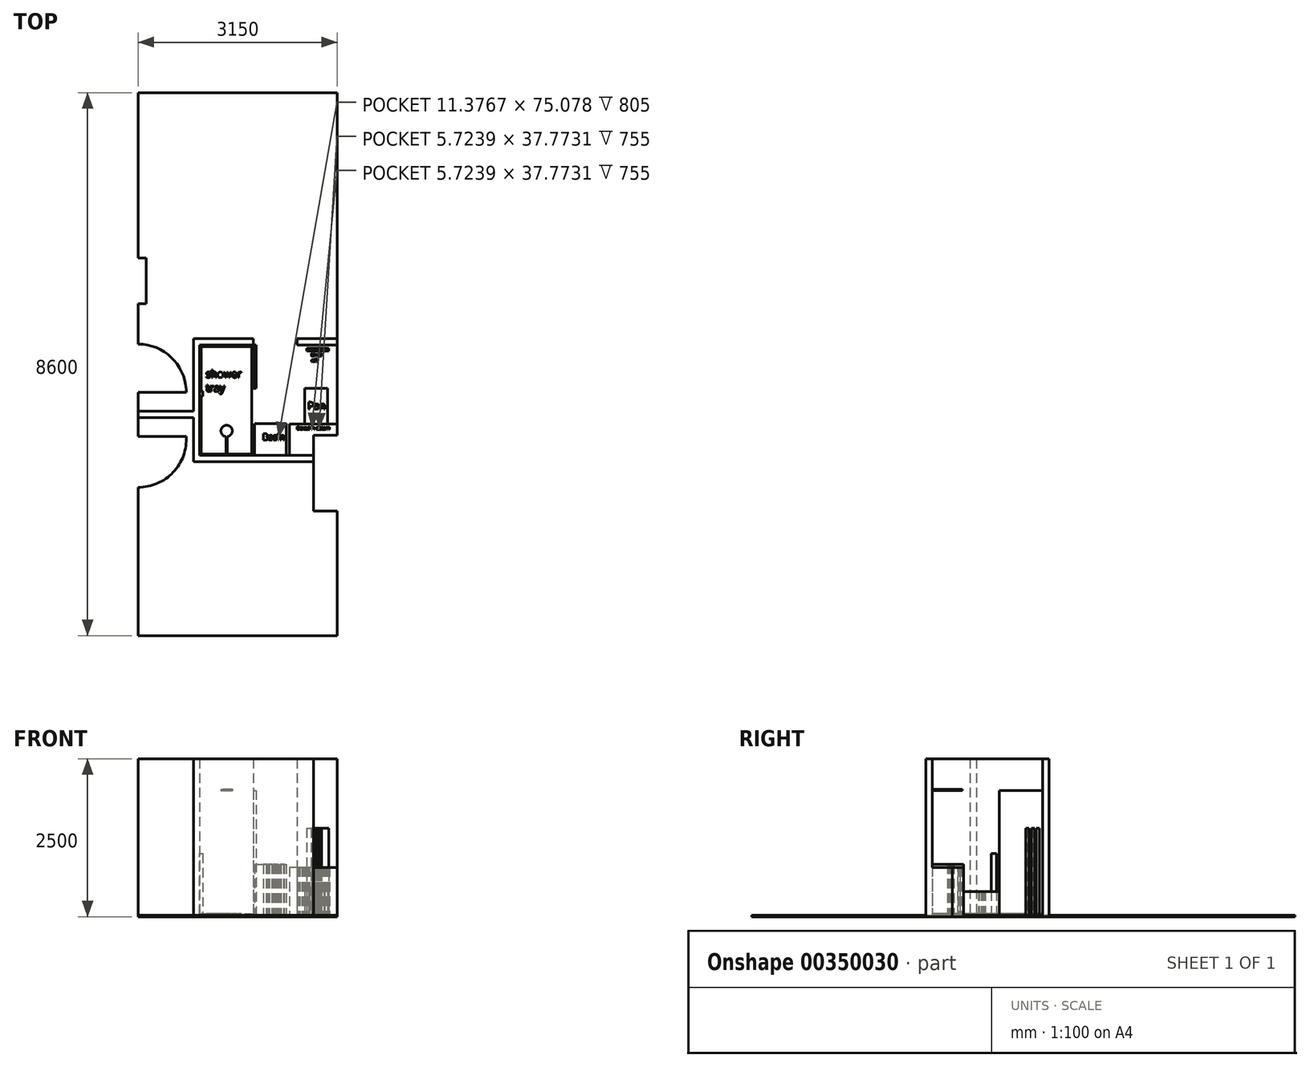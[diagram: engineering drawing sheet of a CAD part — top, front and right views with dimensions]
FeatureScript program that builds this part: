
annotation { "Feature Type Name" : "Feature", "Feature Type Description" : "" }
export const myFeature = defineFeature(function(context is Context, id is Id, definition is map)
    precondition{}
    {
        {
            var Q0;
            Q0=qCreatedBy(makeId("Top.planeOp"),FACE);
            var sketch = newSketch(context, id + "F0", { "sketchPlane" : qUnion([Q0])});
            skLineSegment(sketch, "E0", {"start": v(0, 1108.57) * mm, "end": v(3150, 1108.57) * mm});
            skLineSegment(sketch, "E1", {"start": v(3150, 1108.57) * mm, "end": v(3150, 3083.57) * mm});
            skLineSegment(sketch, "E2", {"start": v(3150, 3083.57) * mm, "end": v(2775, 3083.57) * mm});
            skLineSegment(sketch, "E3", {"start": v(2775, 3083.57) * mm, "end": v(2775, 4283.57) * mm});
            skLineSegment(sketch, "E4", {"start": v(2775, 4283.57) * mm, "end": v(3150, 4283.57) * mm});
            skLineSegment(sketch, "E5", {"start": v(3150, 4283.57) * mm, "end": v(3150, 9708.57) * mm});
            skLineSegment(sketch, "E6", {"start": v(3150, 9708.57) * mm, "end": v(0, 9708.57) * mm});
            skLineSegment(sketch, "E7", {"start": v(0, 9708.57) * mm, "end": v(0, 7088.57) * mm});
            skLineSegment(sketch, "E8", {"start": v(0, 7088.57) * mm, "end": v(125, 7088.57) * mm});
            skLineSegment(sketch, "E9", {"start": v(125, 7088.57) * mm, "end": v(125, 6363.57) * mm});
            skLineSegment(sketch, "E10", {"start": v(125, 6363.57) * mm, "end": v(0, 6363.57) * mm});
            skLineSegment(sketch, "E11", {"start": v(0, 3501.57) * mm, "end": v(0, 1108.57) * mm});
            skLineSegment(sketch, "E12.bottom", {"start": v(0, 4263.57) * mm, "end": v(762, 4263.57) * mm});
            skLineSegment(sketch, "E12.top", {"start": v(0, 4221.57) * mm, "end": v(762, 4221.57) * mm});
            skLineSegment(sketch, "E12.left", {"start": v(0, 4263.57) * mm, "end": v(0, 4221.57) * mm});
            skLineSegment(sketch, "E12.right", {"start": v(762, 4263.57) * mm, "end": v(762, 4221.57) * mm});
            skArc(sketch, "E13", {"start": v(762, 4263.57) * mm, "mid": v(554.28, 3697) * mm, "end": v(0, 3458.41) * mm});
            skLineSegment(sketch, "E14", {"start": v(0, 6363.57) * mm, "end": v(0, 5725.57) * mm});
            skLineSegment(sketch, "E15", {"start": v(0, 4963.57) * mm, "end": v(0, 4263.57) * mm});
            skLineSegment(sketch, "E16.bottom", {"start": v(0, 4963.57) * mm, "end": v(762, 4963.57) * mm});
            skLineSegment(sketch, "E16.top", {"start": v(0, 5005.57) * mm, "end": v(762, 5005.57) * mm});
            skLineSegment(sketch, "E16.left", {"start": v(0, 4963.57) * mm, "end": v(0, 5005.57) * mm});
            skLineSegment(sketch, "E16.right", {"start": v(762, 4963.57) * mm, "end": v(762, 5005.57) * mm});
            skArc(sketch, "E17", {"start": v(762, 4963.57) * mm, "mid": v(538.82, 5502.39) * mm, "end": v(0, 5725.57) * mm});
            skSolve(sketch);
        }
        {
            var Q0;
            Q0=qCreatedBy(makeId("Top.planeOp"),FACE);
            var sketch = newSketch(context, id + "F1", { "sketchPlane" : qUnion([Q0])});
            skLineSegment(sketch, "E18", {"start": v(2775, 3963.57) * mm, "end": v(975, 3963.57) * mm});
            skLineSegment(sketch, "E19", {"start": v(975, 3963.57) * mm, "end": v(975, 5713.57) * mm});
            skLineSegment(sketch, "E20", {"start": v(975, 5713.57) * mm, "end": v(1825, 5713.57) * mm});
            skLineSegment(sketch, "E21.0", {"start": v(875, 3863.57) * mm, "end": v(875, 4563.57) * mm});
            skLineSegment(sketch, "E22.0", {"start": v(2775, 3863.57) * mm, "end": v(875, 3863.57) * mm});
            skLineSegment(sketch, "E23", {"start": v(875, 5813.57) * mm, "end": v(1825, 5813.57) * mm});
            skLineSegment(sketch, "E24", {"start": v(2775, 3963.57) * mm, "end": v(2775, 3863.57) * mm});
            skLineSegment(sketch, "E25.bottom", {"start": v(0, 4663.57) * mm, "end": v(875, 4663.57) * mm});
            skLineSegment(sketch, "E25.top", {"start": v(0, 4563.57) * mm, "end": v(875, 4563.57) * mm});
            skLineSegment(sketch, "E25.left", {"start": v(0, 4663.57) * mm, "end": v(0, 4563.57) * mm});
            skLineSegment(sketch, "E26.trimOffspring", {"start": v(875, 4663.57) * mm, "end": v(875, 5813.57) * mm});
            skLineSegment(sketch, "E27", {"start": v(1825, 5813.57) * mm, "end": v(1825, 5713.57) * mm});
            skSolve(sketch);
        }
        {
            var Q0;
            Q0=qCreatedBy(makeId("Top.planeOp"),FACE);
            var sketch = newSketch(context, id + "F2", { "sketchPlane" : qUnion([Q0])});
            skLineSegment(sketch, "E28.bottom", {"start": v(2515, 5813.57) * mm, "end": v(3150, 5813.57) * mm});
            skLineSegment(sketch, "E28.top", {"start": v(2515, 5713.57) * mm, "end": v(3150, 5713.57) * mm});
            skLineSegment(sketch, "E28.left", {"start": v(2515, 5813.57) * mm, "end": v(2515, 5713.57) * mm});
            skLineSegment(sketch, "E28.right", {"start": v(3150, 5813.57) * mm, "end": v(3150, 5713.57) * mm});
            skSolve(sketch);
        }
        {
            var Q0;
            Q0=qCreatedBy(makeId("Top.planeOp"),FACE);
            cPlane(context, id + "F3", {"entities" : qUnion([Q0]), "cplaneType" : CPlaneType.OFFSET, "offset" : 2000 * mm, "width" : 150 * mm, "height" : 150 * mm});
        }
        {
            var Q0;
            Q0=qCreatedBy(makeId("Top.planeOp"),FACE);
            var sketch = newSketch(context, id + "F4", { "sketchPlane" : qUnion([Q0])});
            skLineSegment(sketch, "E29.bottom", {"start": v(1825, 5713.57) * mm, "end": v(1867, 5713.57) * mm});
            skLineSegment(sketch, "E29.top", {"start": v(1825, 5023.57) * mm, "end": v(1867, 5023.57) * mm});
            skLineSegment(sketch, "E29.left", {"start": v(1825, 5713.57) * mm, "end": v(1825, 5023.57) * mm});
            skLineSegment(sketch, "E29.right", {"start": v(1867, 5713.57) * mm, "end": v(1867, 5023.57) * mm});
            skArc(sketch, "E30", {"start": v(1825, 5023.57) * mm, "mid": v(2312.9, 5225.67) * mm, "end": v(2515, 5713.57) * mm, "construction": true});
            skSolve(sketch);
        }
        {
            var Q0;
            Q0=qCreatedBy(makeId("Top.planeOp"),FACE);
            var sketch = newSketch(context, id + "F5", { "sketchPlane" : qUnion([Q0])});
            skLineSegment(sketch, "E31.bottom", {"start": v(995, 5683.57) * mm, "end": v(1795, 5683.57) * mm});
            skLineSegment(sketch, "E31.top", {"start": v(995, 3983.57) * mm, "end": v(1795, 3983.57) * mm});
            skLineSegment(sketch, "E31.left", {"start": v(995, 5683.57) * mm, "end": v(995, 3983.57) * mm});
            skLineSegment(sketch, "E31.right", {"start": v(1795, 5683.57) * mm, "end": v(1795, 3983.57) * mm});
            skText(sketch, "E32", { "text": "shower\ntray", "fontName": "OpenSans-Regular.ttf"});
            const initialGuessF5  = {"E32": [1.0738, 5.19529, 1, 0, 0.11732]};
            skSetInitialGuess(sketch, initialGuessF5);
            skSolve(sketch);
        }
        {
            var Q0;
            Q0=qCreatedBy(makeId("Top.planeOp"),FACE);
            var sketch = newSketch(context, id + "F6", { "sketchPlane" : qUnion([Q0])});
            skLineSegment(sketch, "E33.bottom", {"start": v(3000, 4458.57) * mm, "end": v(2635, 4458.57) * mm});
            skLineSegment(sketch, "E33.top", {"start": v(3000, 5023.57) * mm, "end": v(2635, 5023.57) * mm});
            skLineSegment(sketch, "E33.left", {"start": v(3000, 4458.57) * mm, "end": v(3000, 5023.57) * mm});
            skLineSegment(sketch, "E33.right", {"start": v(2635, 4458.57) * mm, "end": v(2635, 5023.57) * mm});
            skText(sketch, "E34", { "text": "Pan", "fontName": "OpenSans-Regular.ttf"});
            const initialGuessF6  = {"E34": [2.6861, 4.69488, 1, 0, 0.11267]};
            skSetInitialGuess(sketch, initialGuessF6);
            skSolve(sketch);
        }
        {
            var Q0;
            Q0=qCreatedBy(makeId("Top.planeOp"),FACE);
            var sketch = newSketch(context, id + "F7", { "sketchPlane" : qUnion([Q0])});
            skLineSegment(sketch, "E35.bottom", {"start": v(1845, 3963.57) * mm, "end": v(2345, 3963.57) * mm});
            skLineSegment(sketch, "E35.top", {"start": v(1845, 4463.57) * mm, "end": v(2345, 4463.57) * mm});
            skLineSegment(sketch, "E35.left", {"start": v(1845, 3963.57) * mm, "end": v(1845, 4463.57) * mm});
            skLineSegment(sketch, "E35.right", {"start": v(2345, 3963.57) * mm, "end": v(2345, 4463.57) * mm});
            skText(sketch, "E36", { "text": "Basin", "fontName": "OpenSans-Regular.ttf"});
            const initialGuessF7  = {"E36": [1.96667, 4.20594, 1, 0, 0.10101]};
            skSetInitialGuess(sketch, initialGuessF7);
            skSolve(sketch);
        }
        {
            var Q0;
            Q0=qCreatedBy(makeId("Top.planeOp"),FACE);
            var sketch = newSketch(context, id + "F8", { "sketchPlane" : qUnion([Q0])});
            skLineSegment(sketch, "E37", {"start": v(3150, 4458.57) * mm, "end": v(2395, 4458.57) * mm});
            skLineSegment(sketch, "E38", {"start": v(2395, 4458.57) * mm, "end": v(2395, 3963.57) * mm});
            skText(sketch, "E39", { "text": "Boxed in cistern", "fontName": "OpenSans-Regular.ttf"});
            skLineSegment(sketch, "E40", {"start": v(3150, 4458.57) * mm, "end": v(3150, 4283.57) * mm});
            skLineSegment(sketch, "E41", {"start": v(3150, 4283.57) * mm, "end": v(2775, 4283.57) * mm});
            skLineSegment(sketch, "E42", {"start": v(2775, 4283.57) * mm, "end": v(2775, 3963.57) * mm});
            skLineSegment(sketch, "E43", {"start": v(2775, 3963.57) * mm, "end": v(2395, 3963.57) * mm});
            const initialGuessF8  = {"E39": [2.50984, 4.37021, 1, 0, 0.05082]};
            skSetInitialGuess(sketch, initialGuessF8);
            skSolve(sketch);
        }
        {
            var Q0;
            Q0=qCreatedBy(makeId("Top.planeOp"),FACE);
            var sketch = newSketch(context, id + "F9", { "sketchPlane" : qUnion([Q0])});
            skLineSegment(sketch, "E44.bottom", {"start": v(2670, 5663.57) * mm, "end": v(3020, 5663.57) * mm});
            skLineSegment(sketch, "E44.top", {"start": v(2670, 5613.57) * mm, "end": v(3020, 5613.57) * mm});
            skLineSegment(sketch, "E44.left", {"start": v(2670, 5663.57) * mm, "end": v(2670, 5613.57) * mm});
            skLineSegment(sketch, "E44.right", {"start": v(3020, 5663.57) * mm, "end": v(3020, 5613.57) * mm});
            skText(sketch, "E45", { "text": "towel\nrail", "fontName": "OpenSans-Regular.ttf"});
            const initialGuessF9  = {"E45": [2.73678, 5.53475, 1, 0, 0.04826]};
            skSetInitialGuess(sketch, initialGuessF9);
            skSolve(sketch);
        }
        {
            var Q0;
            Q0=qCreatedBy(id+"F3.planeOp",FACE);
            var sketch = newSketch(context, id + "F10", { "sketchPlane" : qUnion([Q0])});
            skCircle(sketch, "E46", {"center": v(1400, 4351.46) * mm, "radius": 90 * mm});
            skLineSegment(sketch, "E47", {"start": v(1400, 4351.46) * mm, "end": v(1400, 3918.27) * mm});
            skLineSegment(sketch, "E48.0", {"start": v(1410, 4351.46) * mm, "end": v(1410, 3918.27) * mm});
            skLineSegment(sketch, "E49.0", {"start": v(1390, 4351.46) * mm, "end": v(1390, 3918.27) * mm});
            skLineSegment(sketch, "E50", {"start": v(1390, 4351.46) * mm, "end": v(1410, 4351.46) * mm});
            skLineSegment(sketch, "E51", {"start": v(1390, 3918.27) * mm, "end": v(1410, 3918.27) * mm});
            skSolve(sketch);
        }
        {
            var Q0;
            Q0=qCreatedBy(makeId("Top.planeOp"),FACE);
            var sketch = newSketch(context, id + "F11", { "sketchPlane" : qUnion([Q0])});
            skLineSegment(sketch, "E52.bottom", {"start": v(943.25, 4981.3) * mm, "end": v(1023.25, 4981.3) * mm});
            skLineSegment(sketch, "E52.top", {"start": v(943.25, 4901.3) * mm, "end": v(1023.25, 4901.3) * mm});
            skLineSegment(sketch, "E52.left", {"start": v(943.25, 4981.3) * mm, "end": v(943.25, 4901.3) * mm});
            skLineSegment(sketch, "E52.right", {"start": v(1023.25, 4981.3) * mm, "end": v(1023.25, 4901.3) * mm});
            skSolve(sketch);
        }
        {
            var Q0;
            {var subQ0=sQuery(id+"F0.wireOp",EDGE,"E0");Q0=makeQuery(id+"F0.imprint","IMPRINT",FACE,{"disambiguationData":[TD([[makeQuery(id+"F0.imprint","IMPRINT",EDGE,{"derivedFrom":subQ0}),1.0]])]});}
            extrude(context, id + "F12", {"entities" : qUnion([Q0]), "depth" : 25 * mm});
        }
        {
            var Q0;
            Q0 = qSketchRegion(id + "F5", true);
            extrude(context, id + "F13", {"entities" : qUnion([Q0]), "operationType" : NewBodyOperationType.ADD, "depth" : 50 * mm});
        }
        {
            var Q0;
            Q0 = qSketchRegion(id + "F6", true);
            extrude(context, id + "F14", {"entities" : qUnion([Q0]), "operationType" : NewBodyOperationType.ADD, "depth" : 400 * mm});
        }
        {
            var Q0;
            Q0 = qSketchRegion(id + "F7", true);
            extrude(context, id + "F15", {"entities" : qUnion([Q0]), "operationType" : NewBodyOperationType.ADD, "depth" : 830 * mm});
        }
        {
            var Q0;
            Q0 = qSketchRegion(id + "F8", true);
            extrude(context, id + "F16", {"entities" : qUnion([Q0]), "operationType" : NewBodyOperationType.ADD, "depth" : 780 * mm});
        }
        {
            var Q0;
            Q0 = qSketchRegion(id + "F9", true);
            extrude(context, id + "F17", {"entities" : qUnion([Q0]), "operationType" : NewBodyOperationType.ADD, "depth" : 1400 * mm});
        }
        {
            var Q0;
            Q0 = qSketchRegion(id + "F10", true);
            extrude(context, id + "F18", {"entities" : qUnion([Q0]), "operationType" : NewBodyOperationType.ADD, "depth" : 20 * mm, "offsetDistance" : 25 * mm});
        }
        {
            var Q0;
            Q0 = qSketchRegion(id + "F11", true);
            extrude(context, id + "F19", {"entities" : qUnion([Q0]), "operationType" : NewBodyOperationType.ADD, "depth" : 1000 * mm});
        }
        {
            var Q0;
            Q0 = qSketchRegion(id + "F1", true);
            extrude(context, id + "F20", {"entities" : qUnion([Q0]), "operationType" : NewBodyOperationType.ADD, "depth" : 2500 * mm});
        }
        {
            var Q0;
            Q0 = qSketchRegion(id + "F2", true);
            extrude(context, id + "F21", {"entities" : qUnion([Q0]), "operationType" : NewBodyOperationType.ADD, "depth" : 2500 * mm});
        }
        {
            var Q0;
            Q0 = qSketchRegion(id + "F4", true);
            extrude(context, id + "F22", {"entities" : qUnion([Q0]), "depth" : 2000 * mm});
        }
    });
